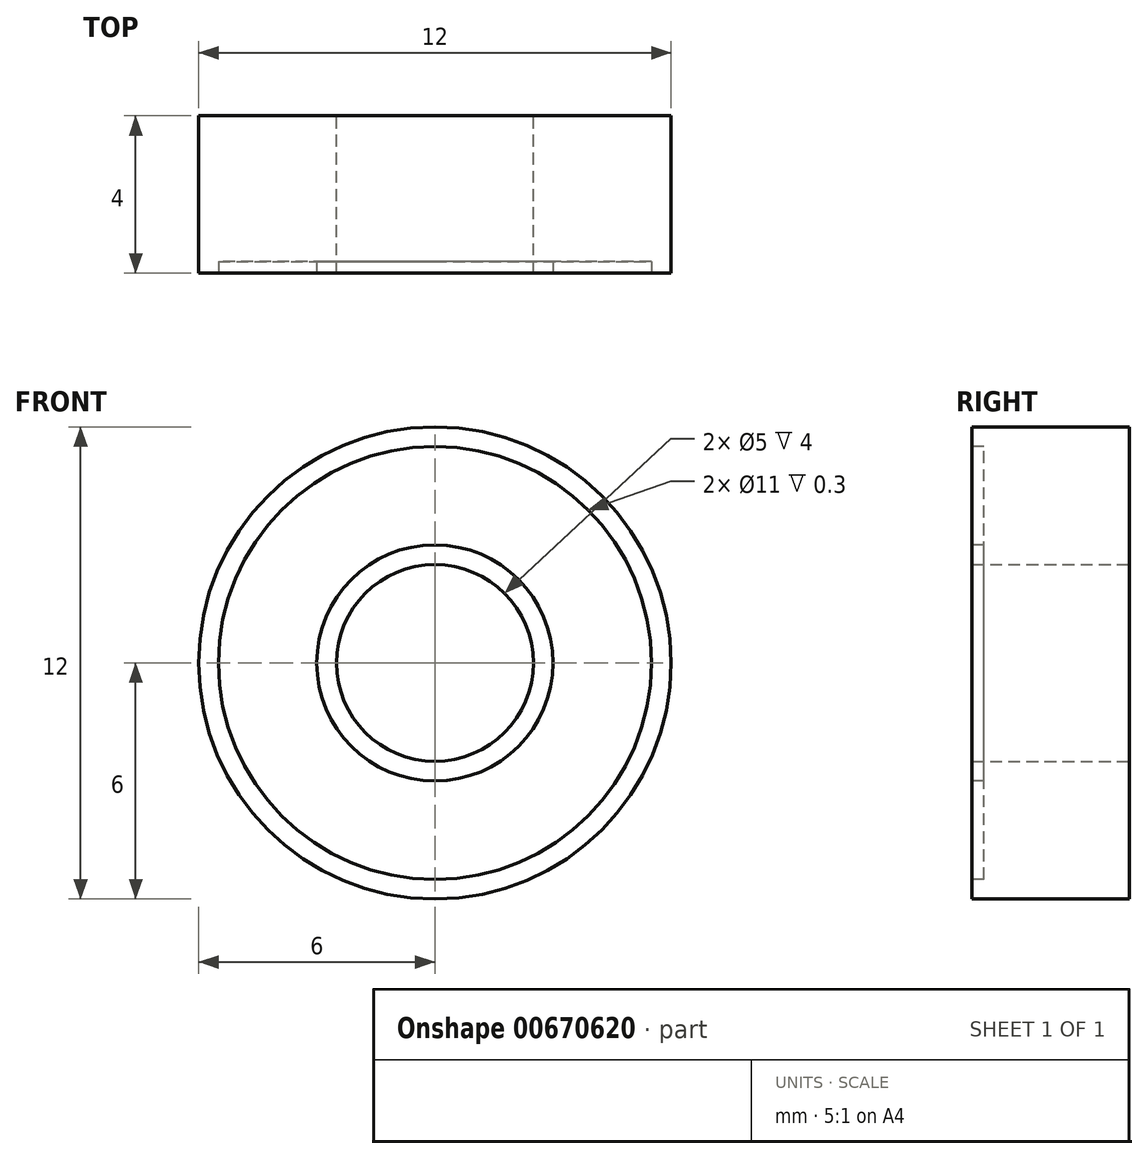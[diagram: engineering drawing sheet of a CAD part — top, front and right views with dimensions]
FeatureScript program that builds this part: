
annotation { "Feature Type Name" : "Feature", "Feature Type Description" : "" }
export const myFeature = defineFeature(function(context is Context, id is Id, definition is map)
    precondition{}
    {
        {
            var Q0;
            Q0=qCreatedBy(makeId("Front.planeOp"),FACE);
            var sketch = newSketch(context, id + "F0", { "sketchPlane" : qUnion([Q0])});
            skCircle(sketch, "E0", {"center": v(0, 0) * mm, "radius": 6 * mm});
            skCircle(sketch, "E1", {"center": v(0, 0) * mm, "radius": 2.5 * mm});
            skSolve(sketch);
        }
        {
            var Q0;
            Q0 = qSketchRegion(id + "F0", true);
            extrude(context, id + "F1", {"entities" : qUnion([Q0]), "endBound" : BoundingType.SYMMETRIC, "depth" : 4 * mm, "offsetDistance" : 25 * mm});
        }
        {
            var Q0;
            Q0=makeQuery(id+"F1.opExtrude","CAP_FACE",FACE,{"disambiguationData":[OSD([sQuery(id+"F0.wireOp",EDGE,"E0"),sQuery(id+"F0.wireOp",EDGE,"E1")])],"isStart":false});
            var sketch = newSketch(context, id + "F2", { "sketchPlane" : qUnion([Q0])});
            skCircle(sketch, "E2", {"center": v(0, 0) * mm, "radius": 5.5 * mm});
            skCircle(sketch, "E3", {"center": v(0, 0) * mm, "radius": 3 * mm});
            skSolve(sketch);
        }
        {
            var Q0;
            Q0 = qSketchRegion(id + "F2", true);
            extrude(context, id + "F3", {"entities" : qUnion([Q0]), "operationType" : NewBodyOperationType.REMOVE, "oppositeDirection" : true, "depth" : 0.3 * mm, "offsetDistance" : 25 * mm});
        }
    });
